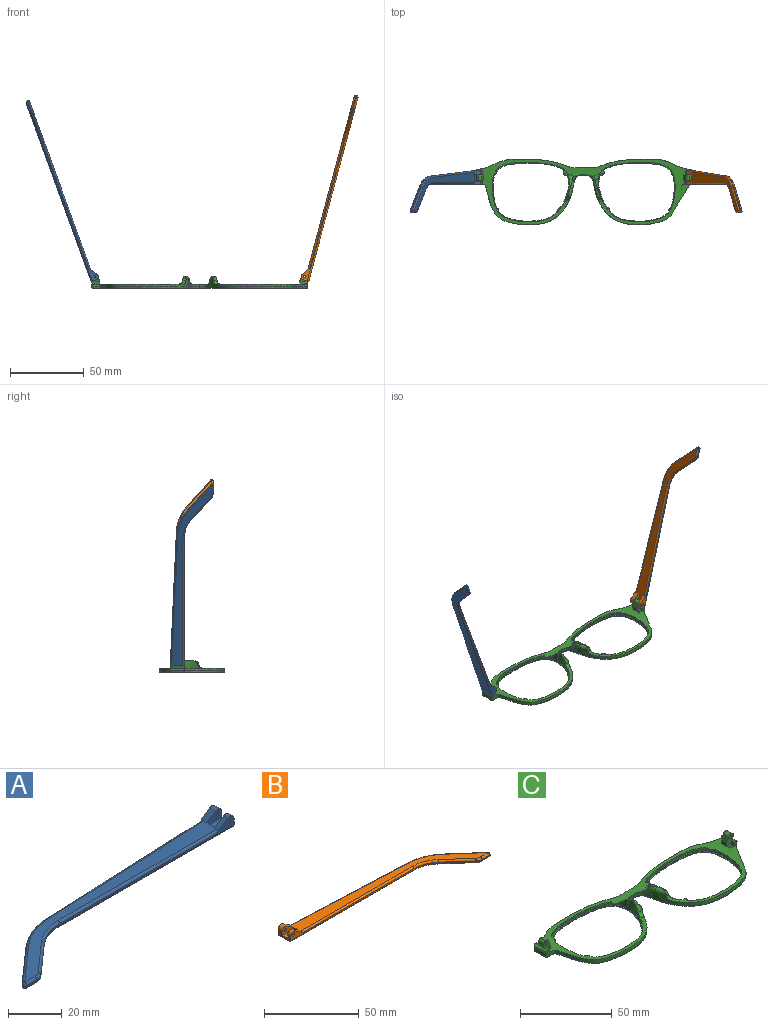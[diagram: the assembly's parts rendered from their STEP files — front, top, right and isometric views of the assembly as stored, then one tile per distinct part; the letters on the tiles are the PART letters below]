
ASSEMBLY  parts=3 mates=2
PART A: 43 faces, bbox 130.2x29.5x5.9 mm
  f0: plane 9.62x3.72mm, normal (1,0,0), area 24.7mm2, adj f1,f3,f4,f5,f10,f16,f18,f28
  f1: cylinder r=2.2mm len=3.45mm, axis (0,-1,0), area 11mm2, adj f0,f2,f4,f37
  f2: plane 6.01x3.91mm, normal (-0.55,0,0.84), area 12.7mm2, adj f1,f4,f9,f19,f37
  f3: plane 2.26x0.1mm, normal (0,0,1), area 0.1mm2, adj f0,f5,f18
  f4: plane 92.1x4.9mm, normal (0,-1,0), area 79.9mm2, adj f0,f1,f2,f14,f19,f36,f42
  f5: plane 93.42x4.13mm, normal (-0.04,1,0), area 64.8mm2, adj f0,f3,f11,f15,f17,f27,f28
  f6: plane 17.82x15.72mm, normal (-0.66,0.75,0), area 14.3mm2, adj f11,f12,f25,f30
  f7: plane 5.46x0.6mm, normal (0,-1,0), area 3.3mm2, adj f12,f13,f23,f32
  f8: plane 14.99x13.23mm, normal (0.66,-0.75,0), area 12mm2, adj f13,f14,f21,f34
  f9: plane 121.18x26.73mm, normal (0,0,1), area 627.7mm2, adj f2,f17,f19,f20,f21,f22,f23,f25
  f10: plane 129.1x27.08mm, normal (0,0,-1), area 686.5mm2, adj f0,f28,f29,f30,f32,f33,f34,f35
  f11: cylinder r=30mm len=18.52mm, axis (0,0,-1), area 12.2mm2, adj f5,f6,f26,f29
  f12: cylinder r=1mm len=1.75mm, axis (0,0,-1), area 1.5mm2, adj f6,f7,f24,f31
  f13: cylinder r=5mm len=3.31mm, axis (0,0,-1), area 2.2mm2, adj f7,f8,f22,f33
  f14: cylinder r=20mm len=13.23mm, axis (0,0,1), area 8.7mm2, adj f4,f8,f20,f35
  f15: plane 5.66x0.25mm, normal (0,0,-1), area 0.7mm2, adj f5,f17,f18
  f16: cylinder r=2.2mm len=3.45mm, axis (0,-1,0), area 14.8mm2, adj f0,f17,f18,f38
  f17: plane 6.01x3.91mm, normal (-0.55,0,0.84), area 16.9mm2, adj f5,f9,f15,f16,f18,f27,f38
  f18: plane 7.92x3.3mm, normal (0,1,0), area 15.9mm2, adj f0,f3,f15,f16,f17,f41
  f19: cylinder r=1mm len=84.18mm, axis (-1,0,0), area 131.4mm2, adj f2,f4,f9,f20
  f20: torus R=21mm, axis (0,0,1), area 23.1mm2, adj f9,f14,f19,f21
  f21: cylinder r=1mm len=15.65mm, axis (-0.75,-0.66,0), area 31.4mm2, adj f8,f9,f20,f22
  f22: torus R=4mm, axis (0,0,1), area 5.3mm2, adj f9,f13,f21,f23
  f23: cylinder r=1mm len=5.46mm, axis (-1,0,0), area 8.6mm2, adj f7,f9,f22,f24
  f24: sphere r=1mm, area 2.4mm2, adj f12,f23,f25
  f25: cylinder r=1mm len=18.48mm, axis (0.75,0.66,0), area 37.3mm2, adj f6,f9,f24,f26
  f26: torus R=29mm, axis (0,0,1), area 31.6mm2, adj f9,f11,f25,f27
  f27: cylinder r=1mm len=85.5mm, axis (1,0.04,0), area 133.5mm2, adj f5,f9,f17,f26
  f28: cylinder r=1mm len=93.46mm, axis (-1,-0.04,0), area 146.9mm2, adj f0,f5,f10,f29
  f29: torus R=29mm, axis (0,0,1), area 31.6mm2, adj f10,f11,f28,f30
  f30: cylinder r=1mm len=18.48mm, axis (-0.75,-0.66,0), area 37.3mm2, adj f6,f10,f29,f31
  f31: sphere r=1mm, area 2.4mm2, adj f12,f30,f32
  f32: cylinder r=1mm len=5.46mm, axis (1,0,0), area 8.6mm2, adj f7,f10,f31,f33
  f33: torus R=4mm, axis (0,0,1), area 5.3mm2, adj f10,f13,f32,f34
  f34: cylinder r=1mm len=15.65mm, axis (0.75,0.66,0), area 31.4mm2, adj f8,f10,f33,f35
  f35: torus R=21mm, axis (0,0,1), area 23.1mm2, adj f10,f14,f34,f36
  f36: cylinder r=1mm len=92.1mm, axis (1,0,0), area 144.7mm2, adj f0,f4,f10,f35
  f37: plane 7.92x4.7mm, normal (0,1,0), area 27mm2, adj f0,f1,f2,f39,f40,f42
  f38: plane 7.92x4.7mm, normal (0,-1,0), area 27mm2, adj f0,f16,f17,f39,f40,f41
  f39: plane 7.92x4.1mm, normal (0,0,1), area 32.5mm2, adj f0,f37,f38,f40
  f40: plane 4.1x1.4mm, normal (1,0,0), area 5.7mm2, adj f9,f37,f38,f39
  f41: cylinder r=0.5mm len=3.1mm, axis (0,-1,0), area 9.7mm2, adj f18,f38
  f42: cylinder r=0.5mm len=2.3mm, axis (0,-1,0), area 7.2mm2, adj f4,f37
PART B: 43 faces, bbox 130.2x29.5x5.9 mm
  f0: plane 9.62x3.72mm, normal (-1,0,0), area 24.7mm2, adj f1,f3,f4,f5,f10,f16,f18,f28
  f1: cylinder r=2.2mm len=3.45mm, axis (0,-1,0), area 11mm2, adj f0,f2,f4,f37
  f2: plane 6.01x3.91mm, normal (0.55,0,0.84), area 12.7mm2, adj f1,f4,f9,f19,f37
  f3: plane 2.26x0.1mm, normal (0,0,1), area 0.1mm2, adj f0,f5,f18
  f4: plane 92.1x4.9mm, normal (0,-1,0), area 78.2mm2, adj f0,f1,f2,f14,f19,f36,f42
  f5: plane 93.42x4.13mm, normal (0.04,1,0), area 64.8mm2, adj f0,f3,f11,f15,f17,f27,f28
  f6: plane 17.82x15.72mm, normal (0.66,0.75,0), area 14.3mm2, adj f11,f12,f25,f30
  f7: plane 5.46x0.6mm, normal (0,-1,0), area 3.3mm2, adj f12,f13,f23,f32
  f8: plane 14.99x13.23mm, normal (-0.66,-0.75,0), area 12mm2, adj f13,f14,f21,f34
  f9: plane 121.18x26.73mm, normal (0,0,1), area 627.7mm2, adj f2,f17,f19,f20,f21,f22,f23,f25
  f10: plane 129.1x27.08mm, normal (0,0,-1), area 686.5mm2, adj f0,f28,f29,f30,f32,f33,f34,f35
  f11: cylinder r=30mm len=18.52mm, axis (0,0,-1), area 12.2mm2, adj f5,f6,f26,f29
  f12: cylinder r=1mm len=1.75mm, axis (0,0,-1), area 1.5mm2, adj f6,f7,f24,f31
  f13: cylinder r=5mm len=3.31mm, axis (0,0,-1), area 2.2mm2, adj f7,f8,f22,f33
  f14: cylinder r=20mm len=13.23mm, axis (0,0,1), area 8.7mm2, adj f4,f8,f20,f35
  f15: plane 5.66x0.25mm, normal (0,0,-1), area 0.7mm2, adj f5,f17,f18
  f16: cylinder r=2.2mm len=3.45mm, axis (0,-1,0), area 14.8mm2, adj f0,f17,f18,f38
  f17: plane 6.01x3.91mm, normal (0.55,0,0.84), area 16.9mm2, adj f5,f9,f15,f16,f18,f27,f38
  f18: plane 7.92x3.3mm, normal (0,1,0), area 14.3mm2, adj f0,f3,f15,f16,f17,f41
  f19: cylinder r=1mm len=84.18mm, axis (1,0,0), area 131.4mm2, adj f2,f4,f9,f20
  f20: torus R=21mm, axis (0,0,1), area 23.1mm2, adj f9,f14,f19,f21
  f21: cylinder r=1mm len=15.65mm, axis (0.75,-0.66,0), area 31.4mm2, adj f8,f9,f20,f22
  f22: torus R=4mm, axis (0,0,1), area 5.3mm2, adj f9,f13,f21,f23
  f23: cylinder r=1mm len=5.46mm, axis (1,0,0), area 8.6mm2, adj f7,f9,f22,f24
  f24: sphere r=1mm, area 2.4mm2, adj f12,f23,f25
  f25: cylinder r=1mm len=18.48mm, axis (-0.75,0.66,0), area 37.3mm2, adj f6,f9,f24,f26
  f26: torus R=29mm, axis (0,0,1), area 31.6mm2, adj f9,f11,f25,f27
  f27: cylinder r=1mm len=85.5mm, axis (-1,0.04,0), area 133.5mm2, adj f5,f9,f17,f26
  f28: cylinder r=1mm len=93.46mm, axis (1,-0.04,0), area 146.9mm2, adj f0,f5,f10,f29
  f29: torus R=29mm, axis (0,0,1), area 31.6mm2, adj f10,f11,f28,f30
  f30: cylinder r=1mm len=18.48mm, axis (0.75,-0.66,0), area 37.3mm2, adj f6,f10,f29,f31
  f31: sphere r=1mm, area 2.4mm2, adj f12,f30,f32
  f32: cylinder r=1mm len=5.46mm, axis (-1,0,0), area 8.6mm2, adj f7,f10,f31,f33
  f33: torus R=4mm, axis (0,0,1), area 5.3mm2, adj f10,f13,f32,f34
  f34: cylinder r=1mm len=15.65mm, axis (-0.75,0.66,0), area 31.4mm2, adj f8,f10,f33,f35
  f35: torus R=21mm, axis (0,0,1), area 23.1mm2, adj f10,f14,f34,f36
  f36: cylinder r=1mm len=92.1mm, axis (-1,0,0), area 144.7mm2, adj f0,f4,f10,f35
  f37: plane 7.92x4.7mm, normal (0,1,0), area 25.4mm2, adj f0,f1,f2,f39,f40,f42
  f38: plane 7.92x4.7mm, normal (0,-1,0), area 25.4mm2, adj f0,f16,f17,f39,f40,f41
  f39: plane 7.92x4.1mm, normal (0,0,1), area 32.5mm2, adj f0,f37,f38,f40
  f40: plane 4.1x1.4mm, normal (-1,0,0), area 5.7mm2, adj f9,f37,f38,f39
  f41: cylinder r=0.88mm len=3.1mm, axis (0,-1,0), area 17mm2, adj f18,f38
  f42: cylinder r=0.88mm len=2.3mm, axis (0,-1,0), area 12.6mm2, adj f4,f37
PART C: 116 faces, bbox 148.1x45.4x17.8 mm
  f0: plane 147.64x45.4mm, normal (0,0,1), area 967.8mm2, adj f1,f13,f14,f15,f16,f17,f18,f19
  f1: plane 1.23x0.04mm, normal (0,0,1), area 0mm2, adj f0,f2,f22
  f2: plane 2.76x2.52mm, normal (0,-1,0), area 3.9mm2, adj f1,f3,f12,f13,f21
  f3: plane 9.65x1.24mm, normal (0,0,1), area 8.2mm2, adj f2,f4,f11,f12,f16,f17,f18,f21
  f4: plane 5.77x5.05mm, normal (0,-1,0), area 17mm2, adj f3,f5,f6,f8,f9,f10,f11,f20
  f5: cylinder r=1.98mm len=4mm, axis (0,-1,0), area 12.4mm2, adj f4,f9,f11,f18
  f6: plane 4x3.31mm, normal (-0.94,0,0.34), area 14.1mm2, adj f4,f7,f8,f18
  f7: plane 4x0.02mm, normal (0.34,0,0.94), area 0.1mm2, adj f6,f18,f19
  f8: cylinder r=1.98mm len=4mm, axis (0,1,0), area 12.4mm2, adj f4,f6,f9,f18
  f9: plane 4x0.01mm, normal (0.34,0,0.94), area 0mm2, adj f4,f5,f8,f18
  f10: cylinder r=0.88mm len=4mm, axis (0,-1,0), area 22mm2, adj f4,f18
  f11: plane 4x2.21mm, normal (0.94,0,-0.34), area 9.4mm2, adj f3,f4,f5,f18
  f12: plane 9.71x1.44mm, normal (0.34,0,0.94), area 13.9mm2, adj f2,f3,f13,f14,f15,f16
  f13: cone r=1mm half-angle=20deg, axis (0,0,1), area 2.3mm2, adj f0,f2,f12,f14
  f14: plane 7.67x1.6mm, normal (0.94,0,-0.34), area 13mm2, adj f0,f12,f13,f15
  f15: cylinder r=1mm len=2.28mm, axis (-0.34,0,-0.94), area 3mm2, adj f0,f12,f14,f16
  f16: plane 2.1x1.69mm, normal (0,1,0), area 2.8mm2, adj f0,f3,f12,f15,f17
  f17: plane 3.3x2.1mm, normal (-1,0,0), area 6.9mm2, adj f0,f3,f16,f18
  f18: plane 6.97x5.07mm, normal (0,1,0), area 22.7mm2, adj f0,f3,f5,f6,f7,f8,f9,f10
  f19: plane 4x2.36mm, normal (-1,0,0), area 9.5mm2, adj f0,f7,f18,f20
  f20: plane 3.2x2.36mm, normal (0,-1,0), area 5.7mm2, adj f0,f4,f19,f21
  f21: plane 2.35x2.1mm, normal (-1,0,0), area 4.9mm2, adj f0,f2,f3,f4,f20
  f22: extruded ~73.43x44.6mm, area 356.2mm2, adj f0,f1,f23,f24,f25,f30,f31,f32
  f23: bspline ~5.37x1.57mm, area 0mm2, adj f22,f24
  f24: extruded ~3.69x2.62mm, area 4.4mm2, adj f22,f23,f25,f53
  f25: bspline ~8.21x5.37mm, area 16.9mm2, adj f22,f24,f26,f30,f53,f65
  f26: bspline ~15.43x15.34mm, area 12.6mm2, adj f25,f27,f28,f61,f64
  f27: extruded ~4.82x0.87mm, area 4.1mm2, adj f26,f61
  f28: plane 3.91x1.2mm, normal (0,0,1), area 2.1mm2, adj f26,f29,f30,f61
  f29: bspline ~7.25x7.25mm, area 9.7mm2, adj f28,f30,f32,f54,f61
  f30: bspline ~9.62x4.5mm, area 16.1mm2, adj f22,f25,f28,f29,f32
  f31: plane 4.27x1.46mm, normal (0,0,1), area 0.2mm2, adj f22,f32
  f32: extruded ~4.23x3.48mm, area 14.9mm2, adj f22,f29,f30,f31,f54
  f33: bspline ~38.99x8.35mm, area 60.6mm2, adj f22,f34,f41,f48
  f34: bspline ~38.11x7mm, area 56.6mm2, adj f33,f35,f41,f115
  f35: bspline ~38.11x7mm, area 56.6mm2, adj f34,f36,f41,f114
  f36: bspline ~39.06x8.36mm, area 60.6mm2, adj f35,f37,f41,f113
  f37: bspline ~1.04x1mm, area 0.7mm2, adj f36,f38,f113
  f38: bspline ~8.99x1.23mm, area 12.6mm2, adj f37,f39,f41,f113
  f39: bspline ~1x1mm, area 0.8mm2, adj f38,f40,f113
  f40: bspline ~72.88x34.91mm, area 168.9mm2, adj f39,f41,f51,f113
  f41: plane 144.79x42.73mm, normal (0,0,-1), area 603.2mm2, adj f33,f34,f35,f36,f38,f40,f42,f45
  f42: bspline ~53.19x41.35mm, area 239.3mm2, adj f41,f43
  f43: plane 52.61x40.82mm, normal (0,0,1), area 83.4mm2, adj f42,f44
  f44: extruded ~52.11x40.52mm, area 154.5mm2, adj f43,f90
  f45: bspline ~53.19x41.35mm, area 239.3mm2, adj f41,f46
  f46: plane 52.61x40.82mm, normal (0,0,1), area 83.4mm2, adj f45,f47
  f47: extruded ~52.11x40.52mm, area 154.5mm2, adj f46,f61
  f48: bspline ~1.04x1mm, area 0.8mm2, adj f22,f33,f49
  f49: bspline ~8.99x1.23mm, area 12.6mm2, adj f22,f41,f48,f50
  f50: bspline ~1x1mm, area 0.8mm2, adj f22,f49,f51
  f51: bspline ~72.88x34.91mm, area 168.9mm2, adj f22,f40,f41,f50
  f52: bspline ~2.34x1.4mm, area 0.5mm2, adj f22,f53,f65,f66
  f53: bspline ~3.1x2.08mm, area 2.5mm2, adj f22,f24,f25,f52,f65
  f54: bspline ~4.46x3.81mm, area 9.8mm2, adj f0,f22,f29,f32,f61
  f55: cylinder r=1.3mm len=2.17mm, axis (0,0,1), area 1.9mm2, adj f0,f56,f61
  f56: plane 2.18x2.04mm, normal (0,0,-1), area 2.3mm2, adj f55,f61
  f57: cylinder r=1.3mm len=2.21mm, axis (0,0,1), area 1.7mm2, adj f0,f58,f61
  f58: plane 2.22x1.68mm, normal (0,0,-1), area 1.9mm2, adj f57,f61
  f59: cylinder r=2.28mm len=3.22mm, axis (0,0,1), area 2mm2, adj f0,f60,f61
  f60: plane 3.25x1.71mm, normal (0,0,-1), area 2.1mm2, adj f59,f61
  f61: extruded ~52.11x40.52mm, area 214.3mm2, adj f0,f26,f27,f28,f29,f47,f54,f55
  f62: plane 4.01x3.33mm, normal (0,0,-1), area 7.7mm2, adj f61,f63
  f63: cylinder r=2.28mm len=3.99mm, axis (0,0,1), area 3.4mm2, adj f0,f61,f62,f64
  f64: bspline ~9.01x4.79mm, area 11.7mm2, adj f0,f26,f61,f63,f65
  f65: bspline ~3.23x3.06mm, area 3.8mm2, adj f0,f25,f52,f53,f64
  f66: bspline ~6.31x2.31mm, area 2.8mm2, adj f0,f22,f52,f67
  f67: bspline ~6.31x2.31mm, area 2.8mm2, adj f0,f66,f68,f113
  f68: bspline ~2.34x1.4mm, area 0.5mm2, adj f67,f69,f80,f113
  f69: bspline ~3.1x2.08mm, area 2.5mm2, adj f68,f70,f78,f80,f113
  f70: bspline ~8.21x5.37mm, area 16.9mm2, adj f69,f71,f76,f78,f80,f113
  f71: bspline ~9.62x4.5mm, area 16.1mm2, adj f70,f72,f73,f75,f113
  f72: plane 3.91x1.2mm, normal (0,0,1), area 2.1mm2, adj f71,f75,f76,f90
  f73: extruded ~4.23x3.48mm, area 14.9mm2, adj f71,f74,f75,f91,f113
  f74: plane 4.27x1.46mm, normal (0,0,1), area 0.2mm2, adj f73,f113
  f75: bspline ~7.25x7.25mm, area 9.7mm2, adj f71,f72,f73,f90,f91
  f76: bspline ~15.43x15.34mm, area 12.6mm2, adj f70,f72,f77,f81,f90
  f77: extruded ~4.82x0.87mm, area 4.1mm2, adj f76,f90
  f78: extruded ~3.69x2.62mm, area 4.4mm2, adj f69,f70,f79,f113
  f79: bspline ~5.37x1.57mm, area 0mm2, adj f78,f113
  f80: bspline ~3.23x3.06mm, area 3.8mm2, adj f0,f68,f69,f70,f81
  f81: bspline ~9.01x4.79mm, area 11.7mm2, adj f0,f76,f80,f82,f90
  f82: cylinder r=2.28mm len=3.99mm, axis (0,0,1), area 3.4mm2, adj f0,f81,f83,f90
  f83: plane 4.01x3.33mm, normal (0,0,-1), area 7.7mm2, adj f82,f90
  f84: cylinder r=2.28mm len=3.22mm, axis (0,0,1), area 2mm2, adj f0,f85,f90
  f85: plane 3.25x1.71mm, normal (0,0,-1), area 2.1mm2, adj f84,f90
  f86: cylinder r=1.3mm len=2.21mm, axis (0,0,1), area 1.7mm2, adj f0,f87,f90
  f87: plane 2.22x1.68mm, normal (0,0,-1), area 1.9mm2, adj f86,f90
  f88: cylinder r=1.3mm len=2.17mm, axis (0,0,1), area 1.9mm2, adj f0,f89,f90
  f89: plane 2.18x2.04mm, normal (0,0,-1), area 2.3mm2, adj f88,f90
  f90: extruded ~52.11x40.52mm, area 214.3mm2, adj f0,f44,f72,f75,f76,f77,f81,f82
  f91: bspline ~4.46x3.81mm, area 9.8mm2, adj f0,f73,f75,f90,f113
  f92: plane 2.35x2.1mm, normal (1,0,0), area 4.9mm2, adj f0,f93,f95,f102,f104
  f93: plane 2.76x2.52mm, normal (0,-1,0), area 3.9mm2, adj f92,f94,f95,f111,f112
  f94: plane 9.71x1.44mm, normal (-0.34,0,0.94), area 13.9mm2, adj f93,f95,f108,f109,f110,f111
  f95: plane 9.65x1.24mm, normal (0,0,1), area 8.2mm2, adj f92,f93,f94,f96,f102,f106,f107,f108
  f96: plane 4x2.21mm, normal (-0.94,0,-0.34), area 9.4mm2, adj f95,f97,f102,f106
  f97: cylinder r=1.98mm len=4mm, axis (0,-1,0), area 12.4mm2, adj f96,f98,f102,f106
  f98: plane 4x0.01mm, normal (-0.34,0,0.94), area 0mm2, adj f97,f99,f102,f106
  f99: cylinder r=1.98mm len=4mm, axis (0,1,0), area 12.4mm2, adj f98,f100,f102,f106
  f100: plane 4x3.31mm, normal (0.94,0,0.34), area 14.1mm2, adj f99,f101,f102,f106
  f101: plane 4x0.02mm, normal (-0.34,0,0.94), area 0.1mm2, adj f100,f105,f106
  f102: plane 5.77x5.06mm, normal (0,-1,0), area 17mm2, adj f92,f95,f96,f97,f98,f99,f100,f103
  f103: cylinder r=0.88mm len=4mm, axis (0,-1,0), area 22mm2, adj f102,f106
  f104: plane 3.2x2.36mm, normal (0,-1,0), area 5.7mm2, adj f0,f92,f102,f105
  f105: plane 4x2.36mm, normal (1,0,0), area 9.5mm2, adj f0,f101,f104,f106
  f106: plane 6.97x5.07mm, normal (0,1,0), area 22.7mm2, adj f0,f95,f96,f97,f98,f99,f100,f101
  f107: plane 3.3x2.1mm, normal (1,0,0), area 6.9mm2, adj f0,f95,f106,f108
  f108: plane 2.1x1.69mm, normal (0,1,0), area 2.8mm2, adj f0,f94,f95,f107,f109
  f109: cylinder r=1mm len=2.28mm, axis (0.34,0,-0.94), area 3mm2, adj f0,f94,f108,f110
  f110: plane 7.67x1.6mm, normal (-0.94,0,-0.34), area 13mm2, adj f0,f94,f109,f111
  f111: cone r=1mm half-angle=20deg, axis (0,0,1), area 2.3mm2, adj f0,f93,f94,f110
  f112: plane 1.23x0.04mm, normal (0,0,1), area 0mm2, adj f0,f93,f113
  f113: extruded ~73.43x44.6mm, area 356.2mm2, adj f0,f22,f36,f37,f38,f39,f40,f67
  f114: extruded ~35.3x5.86mm, area 72.1mm2, adj f0,f35,f113,f115
  f115: extruded ~35.3x5.86mm, area 72.1mm2, adj f0,f22,f34,f114
PLACE A rot(axis=(0,1,0),70deg) t=(-84.77,-5.75,56)mm
PLACE B rot(axis=(0,-1,0),75deg) t=(68.2,-5.75,-61.61)mm
PLACE C t=(10.15,-1.13,-5.77)mm
MATE revolute A.f1 <-> C.f99  axis (0,-1,0) through (-60.89,2.72,1.22)mm
MATE revolute B.f41 <-> C.f5  axis (0,-1,0) through (81.2,2.72,1.21)mm
